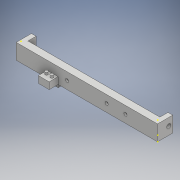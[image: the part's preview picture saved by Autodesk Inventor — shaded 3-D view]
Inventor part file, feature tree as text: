
AUTODESK INVENTOR PART (.ipt)
format: ipt  version: 2018 (Build 220112000, 112)  size: 287,744 bytes
history: native  units: mm
features: sketch x22, extrude x18, fillet x4
ambient origin geometry x8: Origin, YZ Plane, XZ Plane, XY Plane, X Axis, Y Axis, Z Axis, Center Point
bodies: Solid1 (feature_tree)
feature tree (44):
  extrude  "Extrusion1"  Depth=19.925mm
  extrude  "Extrusion2"  Depth=5.0mm
  extrude  "Extrusion3"  Depth=12.175mm TaperAngle=0.0deg
  extrude  "Extrusion4"  Depth=4.65mm TaperAngle=0.0deg
  sketch  "Sketch5"  dims[d11=10.5mm d12=2.75mm]
  extrude  "Extrusion5"  Depth=2.75mm
  extrude  "Extrusion6"  Depth=3.5mm
  extrude  "Extrusion7"  Depth=4.5mm
  fillet  "Fillet1"  Radius=5.0mm
  fillet  "Fillet2"  Radius=3.8mm
  extrude  "Extrusion8"  Depth=3.0mm
  extrude  "Extrusion9"  Depth=3.3mm
  fillet  "Fillet3"  Radius=21.0mm
  extrude  "Extrusion10"  Depth=4.0mm TaperAngle=0.0deg
  sketch  "Sketch12"  dims[d36=3.3mm d37=4.0mm d38=0.0mm]
  sketch  "Sketch13"  dims[d39=3.3mm d40=4.0mm d41=0.0mm]
  extrude  "Extrusion11"  Depth=4.0mm TaperAngle=0.0deg
  extrude  "Extrusion12"  Depth=9.5mm
  extrude  "Extrusion13"  Depth=11.5mm
  sketch  "Sketch16"  dims[d46=9.5mm d47=0.0mm d48=4.0mm]
  sketch  "Sketch17"  dims[d49=6.175mm d50=0.0mm d51=1.825mm d52=0.0mm]
  extrude  "Extrusion14"  Depth=4.0mm
  extrude  "Extrusion15"  Depth=1.825mm TaperAngle=0.0deg
  extrude  "Extrusion16"  Depth=4.5mm TaperAngle=0.0deg
  extrude  "Extrusion17"  Depth=9.5mm TaperAngle=0.0deg
  extrude  "Extrusion18"  Depth=7.5mm
  fillet  "Fillet4"  Radius=2.88mm
  sketch  "Sketch1"  dims[d0=150.0mm d1=19.925mm]
  sketch  "Sketch2"  dims[d2=4.0mm d3=0.0mm d4=5.0mm]
  sketch  "Sketch3"  dims[d5=5.0mm d6=12.175mm d7=0.0mm]
  sketch  "Sketch4"  dims[d8=3.2mm d9=4.65mm d10=0.0mm]
  sketch  "Sketch6"  dims[d13=3.5mm d14=0.0mm d15=7.95mm]
  sketch  "Sketch7"  dims[d16=7.95mm d17=4.5mm]
  sketch  "Sketch8"  dims[d18=155.75mm d19=5.75mm d20=0.0mm d21=0.0mm]
  sketch  "Sketch9"  dims[d22=21.0mm d23=34.875mm d24=0.0mm d25=0.0mm d26=5.0mm d27=3.8mm d28=0.0mm]
  sketch  "Sketch10"  dims[d29=3.0mm d30=3.0mm]
  sketch  "Sketch11"  dims[d33=21.0mm d34=3.3mm d35=21.0mm]
  sketch  "Sketch14"  dims[d42=2.0mm d43=9.5mm]
  sketch  "Sketch15"  dims[d44=5.0mm d45=11.5mm]
  sketch  "Sketch18"  dims[d53=0.5mm d54=0.0mm d55=4.5mm d56=0.0mm]
  sketch  "Sketch19"  dims[d57=4.0mm d58=9.5mm d59=0.0mm]
  sketch  "Sketch20"  dims[d60=7.5mm d61=2.88mm d62=2.88mm]
  sketch  "Sketch21"  dims[d63=3.0mm]
  sketch  "Sketch22"  dims[d64=3.0mm d65=2.5mm d66=0.0mm d67=2.5mm d68=3.0mm d69=0.0mm d70=2.0mm d71=2.5mm d72=0.0mm d73=1.0mm]
